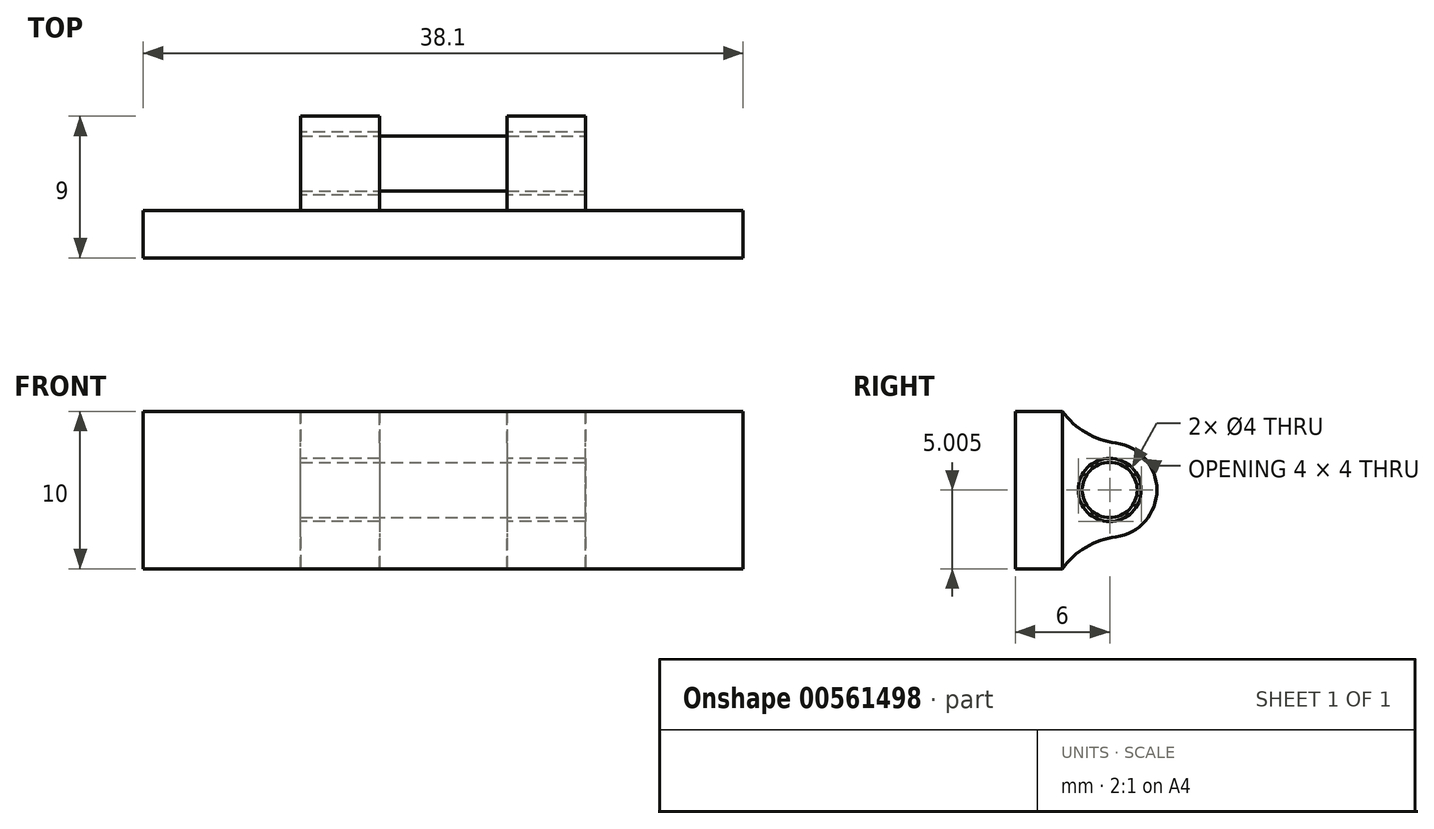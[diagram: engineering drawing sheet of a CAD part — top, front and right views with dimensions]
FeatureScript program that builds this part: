
annotation { "Feature Type Name" : "Feature", "Feature Type Description" : "" }
export const myFeature = defineFeature(function(context is Context, id is Id, definition is map)
    precondition{}
    {
        {
            var Q0;
            Q0=qCreatedBy(makeId("Right.planeOp"),FACE);
            var sketch = newSketch(context, id + "F0", { "sketchPlane" : qUnion([Q0])});
            skLineSegment(sketch, "E0.bottom", {"start": v(-3, 3.28) * mm, "end": v(0, 3.28) * mm});
            skLineSegment(sketch, "E0.top", {"start": v(-3, -6.72) * mm, "end": v(0, -6.72) * mm});
            skLineSegment(sketch, "E0.left", {"start": v(-3, 3.28) * mm, "end": v(-3, -6.72) * mm});
            skLineSegment(sketch, "E0.right", {"start": v(0, 3.28) * mm, "end": v(0, 1.28) * mm});
            skCircle(sketch, "E1", {"center": v(3, -1.72) * mm, "radius": 2 * mm});
            skPoint(sketch, "E1.centerSnap0", {"position": v(0, -1.72) * mm});
            skArc(sketch, "E2.0", {"start": v(2.98, -4.72) * mm, "mid": v(6, -1.73) * mm, "end": v(3, 1.28) * mm});
            skLineSegment(sketch, "E3", {"start": v(0, 1.28) * mm, "end": v(3, 1.28) * mm});
            skLineSegment(sketch, "E4", {"start": v(2.98, -4.72) * mm, "end": v(0, -4.72) * mm});
            skLineSegment(sketch, "E5.trimOffspring", {"start": v(0, -4.72) * mm, "end": v(0, -6.72) * mm});
            skSolve(sketch);
        }
        {
            var Q0;
            Q0=makeQuery(id+"F0.imprint","IMPRINT",FACE,{"disambiguationData":[TD([[makeQuery(id+"F0.imprint","IMPRINT",EDGE,{"derivedFrom":sQuery(id+"F0.wireOp",EDGE,"E0.bottom")}),-1.0]])]});
            extrude(context, id + "F1", {"entities" : qUnion([Q0]), "depth" : 38.1 * mm, "offsetDistance" : 25 * mm});
        }
        {
            var Q0;
            Q0=makeQuery(id+"F1.opExtrude","SWEPT_FACE",FACE,{"disambiguationData":[OSD([sQuery(id+"F0.wireOp",EDGE,"E0.bottom")])]});
            var sketch = newSketch(context, id + "F2", { "sketchPlane" : qUnion([Q0])});
            skLineSegment(sketch, "E6.bottom", {"start": v(0, 0) * mm, "end": v(10, 0) * mm});
            skLineSegment(sketch, "E6.top", {"start": v(0, 7.35) * mm, "end": v(10, 7.35) * mm});
            skLineSegment(sketch, "E6.left", {"start": v(0, 0) * mm, "end": v(0, 7.35) * mm});
            skLineSegment(sketch, "E6.right", {"start": v(10, 0) * mm, "end": v(10, 7.35) * mm});
            skLineSegment(sketch, "E7.bottom", {"start": v(38.1, 0) * mm, "end": v(28.1, 0) * mm});
            skLineSegment(sketch, "E7.top", {"start": v(38.1, 11.29) * mm, "end": v(28.1, 11.29) * mm});
            skLineSegment(sketch, "E7.left", {"start": v(38.1, 0) * mm, "end": v(38.1, 11.29) * mm});
            skLineSegment(sketch, "E7.right", {"start": v(28.1, 0) * mm, "end": v(28.1, 11.29) * mm});
            skSolve(sketch);
        }
        {
            var Q0;
            Q0=qSketchRegion(id+"F2",true);
            extrude(context, id + "F3", {"entities" : qUnion([Q0]), "operationType" : NewBodyOperationType.REMOVE, "oppositeDirection" : true, "depth" : 25 * mm, "offsetDistance" : 25 * mm});
        }
        {
            var Q0;
            Q0=makeQuery(id+"FRlLoRhgsL2sgzW_1.opFillet","SPLIT",FACE,{"disambiguationData":[OD(0.0)],"derivedFrom":makeQuery(id+"F3.boolean.opBoolean","MERGE",FACE,{"derivedFrom":[makeQuery(id+"F1.opExtrude","SWEPT_FACE",FACE,{"disambiguationData":[OSD([sQuery(id+"F0.wireOp",EDGE,"E0.right")])]}),makeQuery(id+"F1.opExtrude","SWEPT_FACE",FACE,{"disambiguationData":[OSD([sQuery(id+"F0.wireOp",EDGE,"E5.trimOffspring")])]}),makeQuery(id+"F3.opExtrude","SWEPT_FACE",FACE,{"disambiguationData":[OSD([sQuery(id+"F2.wireOp",EDGE,"E6.bottom")])]}),makeQuery(id+"F3.opExtrude","SWEPT_FACE",FACE,{"disambiguationData":[OSD([sQuery(id+"F2.wireOp",EDGE,"E7.bottom")])]})]})});
            var sketch = newSketch(context, id + "F4", { "sketchPlane" : qUnion([Q0])});
            skLineSegment(sketch, "E8.bottom", {"start": v(-23.1, 1.26) * mm, "end": v(-15, 1.26) * mm});
            skLineSegment(sketch, "E8.top", {"start": v(-23.1, -4.69) * mm, "end": v(-15, -4.69) * mm});
            skLineSegment(sketch, "E8.left", {"start": v(-23.1, 1.26) * mm, "end": v(-23.1, -4.69) * mm});
            skLineSegment(sketch, "E8.right", {"start": v(-15, 1.26) * mm, "end": v(-15, -4.69) * mm});
            skSolve(sketch);
        }
        {
            var Q0;
            Q0=qSketchRegion(id+"F4",true);
            extrude(context, id + "F5", {"entities" : qUnion([Q0]), "operationType" : NewBodyOperationType.REMOVE, "endBound" : BoundingType.THROUGH_ALL, "depth" : 25 * mm, "offsetDistance" : 25 * mm});
        }
        {
            var Q0;
            Q0=makeQuery(id+"F3.boolean.opBoolean","COPY",FACE,{"derivedFrom":makeQuery(id+"F3.opExtrude","SWEPT_FACE",FACE,{"disambiguationData":[OSD([sQuery(id+"F2.wireOp",EDGE,"E7.right")])]})});
            var sketch = newSketch(context, id + "F6", { "sketchPlane" : qUnion([Q0])});
            skCircle(sketch, "E9", {"center": v(3, -1.72) * mm, "radius": 1.75 * mm});
            skSolve(sketch);
        }
        {
            var Q0;
            Q0=qSketchRegion(id+"F6",true);
            var Q1;
            Q1=makeQuery(id+"F3.boolean.opBoolean","COPY",FACE,{"derivedFrom":makeQuery(id+"F3.opExtrude","SWEPT_FACE",FACE,{"disambiguationData":[OSD([sQuery(id+"F2.wireOp",EDGE,"E6.right")])]})});
            extrude(context, id + "F7", {"entities" : qUnion([Q0]), "endBound" : BoundingType.UP_TO_SURFACE, "oppositeDirection" : true, "depth" : 17.8 * mm, "endBoundEntityFace" : qUnion([Q1]), "offsetDistance" : 25 * mm});
        }
        {
            var Q0;
            Q0=makeQuery(id+"F5.boolean.opBoolean","COPY",FACE,{"derivedFrom":makeQuery(id+"F5.opExtrude","SWEPT_FACE",FACE,{"disambiguationData":[OSD([sQuery(id+"F4.wireOp",EDGE,"E8.top")])]})});
            extrude(context, id + "F8", {"entities" : qUnion([Q0]), "operationType" : NewBodyOperationType.REMOVE, "oppositeDirection" : true, "depth" : 25 * mm, "offsetDistance" : 25 * mm});
        }
        {
            var Q0;
            Q0=makeQuery(id+"F5.boolean.opBoolean","COPY",FACE,{"derivedFrom":makeQuery(id+"F5.opExtrude","SWEPT_FACE",FACE,{"disambiguationData":[OSD([sQuery(id+"F4.wireOp",EDGE,"E8.bottom")])]})});
            extrude(context, id + "F9", {"entities" : qUnion([Q0]), "operationType" : NewBodyOperationType.REMOVE, "oppositeDirection" : true, "depth" : 25 * mm, "offsetDistance" : 25 * mm});
        }
        {
            var Q0;
            {var subQ0=sQuery(id+"F0.wireOp",EDGE,"E4");var subQ1=sQuery(id+"F0.wireOp",EDGE,"E5.trimOffspring");Q0=makeQuery(id+"F8.boolean.opBoolean","SPLIT",EDGE,{"disambiguationData":[TD([makeQuery(id+"F3.boolean.opBoolean","COPY",FACE,{"derivedFrom":makeQuery(id+"F3.opExtrude","SWEPT_FACE",FACE,{"disambiguationData":[OSD([sQuery(id+"F2.wireOp",EDGE,"E7.right")])]})})])],"derivedFrom":makeQuery(id+"F1.opExtrude","SWEPT_EDGE",EDGE,{"disambiguationData":[OSD([subQ0,subQ1])]})});}
            var Q1;
            {var subQ0=sQuery(id+"F0.wireOp",EDGE,"E4");var subQ3=sQuery(id+"F0.wireOp",EDGE,"E5.trimOffspring");Q1=makeQuery(id+"F8.boolean.opBoolean","SPLIT",EDGE,{"disambiguationData":[TD([makeQuery(id+"F3.boolean.opBoolean","COPY",FACE,{"derivedFrom":makeQuery(id+"F3.opExtrude","SWEPT_FACE",FACE,{"disambiguationData":[OSD([sQuery(id+"F2.wireOp",EDGE,"E6.right")])]})})])],"derivedFrom":makeQuery(id+"F1.opExtrude","SWEPT_EDGE",EDGE,{"disambiguationData":[OSD([subQ0,subQ3])]})});}
            var Q2;
            {var subQ3=sQuery(id+"F0.wireOp",EDGE,"E0.right");var subQ4=sQuery(id+"F0.wireOp",EDGE,"E3");Q2=makeQuery(id+"F9.boolean.opBoolean","SPLIT",EDGE,{"disambiguationData":[TD([makeQuery(id+"F3.boolean.opBoolean","COPY",FACE,{"derivedFrom":makeQuery(id+"F3.opExtrude","SWEPT_FACE",FACE,{"disambiguationData":[OSD([sQuery(id+"F2.wireOp",EDGE,"E6.right")])]})})])],"derivedFrom":makeQuery(id+"F1.opExtrude","SWEPT_EDGE",EDGE,{"disambiguationData":[OSD([subQ3,subQ4])]})});}
            var Q3;
            {var subQ3=sQuery(id+"F0.wireOp",EDGE,"E0.right");var subQ4=sQuery(id+"F0.wireOp",EDGE,"E3");Q3=makeQuery(id+"F9.boolean.opBoolean","SPLIT",EDGE,{"disambiguationData":[TD([makeQuery(id+"F3.boolean.opBoolean","COPY",FACE,{"derivedFrom":makeQuery(id+"F3.opExtrude","SWEPT_FACE",FACE,{"disambiguationData":[OSD([sQuery(id+"F2.wireOp",EDGE,"E7.right")])]})})])],"derivedFrom":makeQuery(id+"F1.opExtrude","SWEPT_EDGE",EDGE,{"disambiguationData":[OSD([subQ3,subQ4])]})});}
            fillet(context, id + "F10", {"entities" : qUnion([Q0, Q1, Q2, Q3]), "radius" : 5 * mm, "tangentPropagation" : true, "allowEdgeOverflow" : false});
        }
    });
